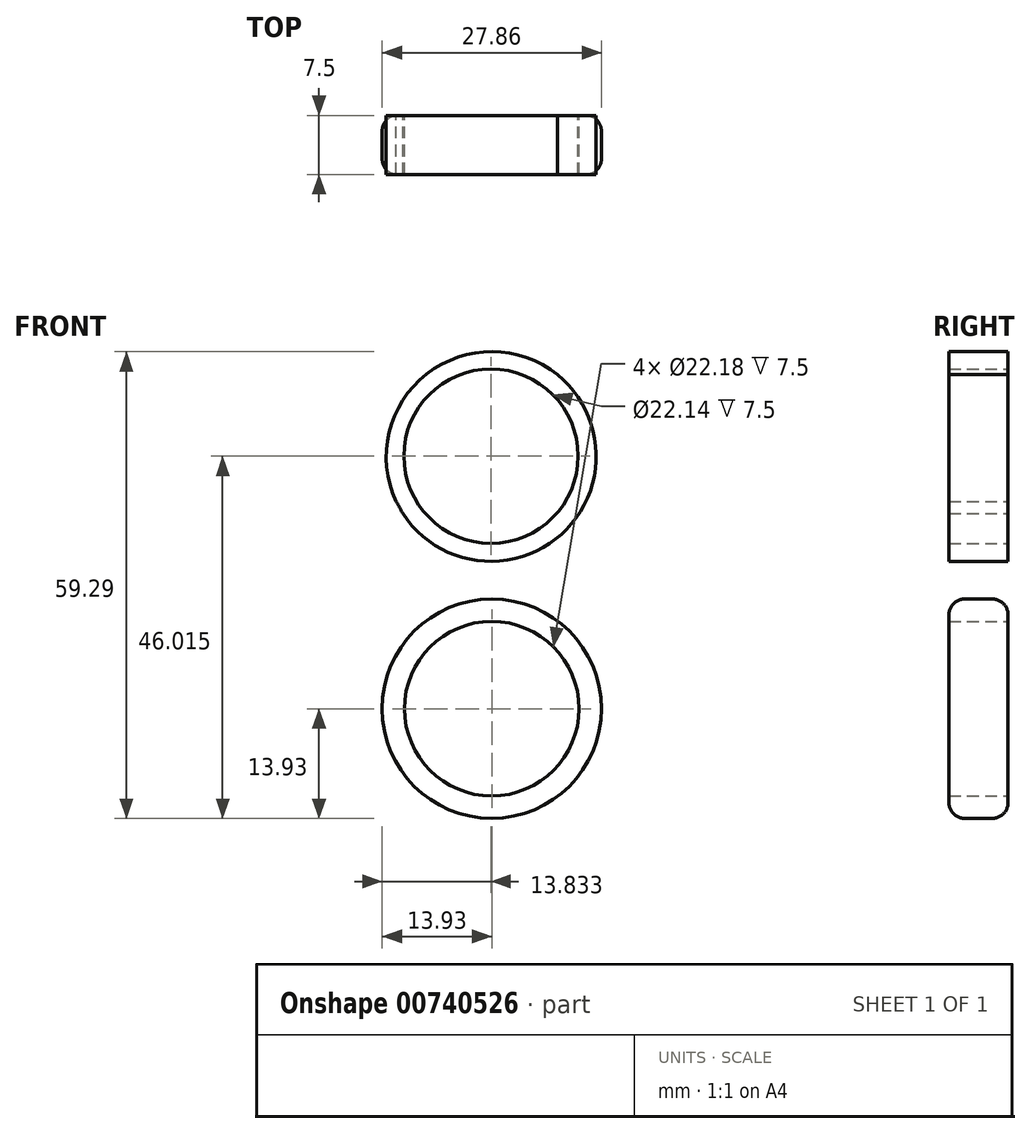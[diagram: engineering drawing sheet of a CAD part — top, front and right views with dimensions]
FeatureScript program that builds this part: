
annotation { "Feature Type Name" : "Feature", "Feature Type Description" : "" }
export const myFeature = defineFeature(function(context is Context, id is Id, definition is map)
    precondition{}
    {
        {
            var Q0;
            Q0=qCreatedBy(makeId("Front.planeOp"),FACE);
            var sketch = newSketch(context, id + "F0", { "sketchPlane" : qUnion([Q0])});
            skCircle(sketch, "E0", {"center": v(0, 0) * mm, "radius": 11.09 * mm});
            skCircle(sketch, "E1", {"center": v(0, 0) * mm, "radius": 13.93 * mm});
            skPoint(sketch, "E2.orphan", {"position": v(-13.93, 6.55) * mm});
            skPoint(sketch, "E3.first.point", {"position": v(-12.25, 30.96) * mm});
            skPoint(sketch, "E3.second.point", {"position": v(12.04, 33.37) * mm});
            skPoint(sketch, "E3.third.point", {"position": v(5.26, 21.12) * mm});
            skCircle(sketch, "E4", {"center": v(-0.1, 32.09) * mm, "radius": 11.07 * mm});
            skCircle(sketch, "E5", {"center": v(-0.1, 32.09) * mm, "radius": 13.37 * mm});
            skArc(sketch, "E6", {"start": v(-11.7, 7.56) * mm, "mid": v(-9.36, 17) * mm, "end": v(-12.16, 26.32) * mm});
            skPoint(sketch, "E6.startSnap0", {"position": v(-13.17, 7.56) * mm});
            skPoint(sketch, "E7.trimOffspring.end.orphan", {"position": v(-8.26, 23) * mm});
            skPoint(sketch, "E8.orphan", {"position": v(-10.96, 11.31) * mm});
            skPoint(sketch, "E9.orphan", {"position": v(10.96, 11.31) * mm});
            skPoint(sketch, "E10.MirrorCS.end.orphan", {"position": v(13.93, 3.28) * mm});
            skPoint(sketch, "E11.MirrorCS.end.orphan", {"position": v(8.26, 23) * mm});
            skArc(sketch, "E12.MirrorCS", {"start": v(11.7, 7.56) * mm, "mid": v(9.36, 17) * mm, "end": v(12.16, 26.32) * mm});
            skArc(sketch, "E13", {"start": v(12.16, 26.32) * mm, "mid": v(0, 45.36) * mm, "end": v(-12.16, 26.32) * mm});
            skArc(sketch, "E14", {"start": v(-11.7, 7.56) * mm, "mid": v(0, -12.58) * mm, "end": v(11.7, 7.56) * mm});
            skPoint(sketch, "E15.end.orphan", {"position": v(-13.93, 3.28) * mm});
            skPoint(sketch, "E15.start.orphan", {"position": v(-13.93, 0) * mm});
            skPoint(sketch, "E16.MirrorCS.start.orphan", {"position": v(13.93, 0) * mm});
            skSolve(sketch);
        }
        {
            var Q0;
            {var subQ0=sQuery(id+"F0.wireOp",EDGE,"E12.MirrorCS");Q0=makeQuery(id+"F0.imprint","IMPRINT",FACE,{"disambiguationData":[TD([[makeQuery(id+"F0.imprint","IMPRINT",EDGE,{"derivedFrom":subQ0}),1.0]])]});}
            var Q1;
            Q1=makeQuery(id+"F0.imprint","IMPRINT",FACE,{"disambiguationData":[TD([[makeQuery(id+"F0.imprint","IMPRINT",EDGE,{"derivedFrom":sQuery(id+"F0.wireOp",EDGE,"E4")}),-1.0]])]});
            var Q2;
            Q2=makeQuery(id+"F0.imprint","IMPRINT",FACE,{"disambiguationData":[TD([[makeQuery(id+"F0.imprint","IMPRINT",EDGE,{"derivedFrom":sQuery(id+"F0.wireOp",EDGE,"E0")}),-1.0]])]});
            var Q3;
            {var subQ0=sQuery(id+"F0.wireOp",EDGE,"E14");Q3=makeQuery(id+"F0.imprint","IMPRINT",FACE,{"disambiguationData":[TD([[makeQuery(id+"F0.imprint","IMPRINT",EDGE,{"derivedFrom":subQ0}),-1.0]])]});}
            extrude(context, id + "F1", {"entities" : qUnion([Q0, Q1, Q2, Q3]), "depth" : 7.5 * mm, "offsetDistance" : 25 * mm});
        }
        {
            var Q0;
            Q0=makeQuery(id+"F1.opExtrude","CAP_EDGE",EDGE,{"disambiguationData":[OSD([sQuery(id+"F0.wireOp",EDGE,"E13")])],"isStart":false});
            var Q1;
            Q1=makeQuery(id+"F1.opExtrude","CAP_EDGE",EDGE,{"disambiguationData":[OSD([sQuery(id+"F0.wireOp",EDGE,"E12.MirrorCS")])],"isStart":false});
            var Q2;
            Q2=makeQuery(id+"F1.opExtrude","CAP_EDGE",EDGE,{"disambiguationData":[OSD([sQuery(id+"F0.wireOp",EDGE,"E6")])],"isStart":false});
            var Q3;
            Q3=makeQuery(id+"F1.opExtrude","CAP_EDGE",EDGE,{"disambiguationData":[OSD([sQuery(id+"F0.wireOp",EDGE,"E1")])],"isStart":false});
            var Q4;
            Q4=makeQuery(id+"F1.opExtrude","CAP_EDGE",EDGE,{"disambiguationData":[OSD([sQuery(id+"F0.wireOp",EDGE,"E6")])],"isStart":true});
            var Q5;
            Q5=makeQuery(id+"F1.opExtrude","CAP_EDGE",EDGE,{"disambiguationData":[OSD([sQuery(id+"F0.wireOp",EDGE,"E1")])],"isStart":true});
            var Q6;
            Q6=makeQuery(id+"F1.opExtrude","CAP_EDGE",EDGE,{"disambiguationData":[OSD([sQuery(id+"F0.wireOp",EDGE,"E12.MirrorCS")])],"isStart":true});
            var Q7;
            Q7=makeQuery(id+"F1.opExtrude","CAP_EDGE",EDGE,{"disambiguationData":[OSD([sQuery(id+"F0.wireOp",EDGE,"E13")])],"isStart":true});
            fillet(context, id + "F2", {"entities" : qUnion([Q0, Q1, Q2, Q3, Q4, Q5, Q6, Q7]), "radius" : 2 * mm, "tangentPropagation" : true, "allowEdgeOverflow" : false});
        }
        {
            var Q0;
            Q0=makeQuery(id+"F1.opExtrude","SWEPT_BODY",BODY,{"disambiguationData":[OSD([sQuery(id+"F0.wireOp",EDGE,"E0"),sQuery(id+"F0.wireOp",EDGE,"E1"),sQuery(id+"F0.wireOp",EDGE,"E4"),sQuery(id+"F0.wireOp",EDGE,"E6"),sQuery(id+"F0.wireOp",EDGE,"E12.MirrorCS"),sQuery(id+"F0.wireOp",EDGE,"E13")])]});
            var Q1;
            Q1=makeQuery(id+"F1.opExtrude","CAP_EDGE",EDGE,{"disambiguationData":[OSD([sQuery(id+"F0.wireOp",EDGE,"E0")])],"isStart":false});
            transform(context, id + "F3", {"entities" : qUnion([Q0]), "transformType" : TransformType.ROTATION, "transformAxis" : qUnion([Q1]), "angle" : 90 * degree, "makeCopy" : true});
        }
        {
            var Q0;
            Q0=makeQuery(id+"F3.opPattern","COPY",BODY,{"derivedFrom":makeQuery(id+"F1.opExtrude","SWEPT_BODY",BODY,{"disambiguationData":[OSD([sQuery(id+"F0.wireOp",EDGE,"E0"),sQuery(id+"F0.wireOp",EDGE,"E1"),sQuery(id+"F0.wireOp",EDGE,"E4"),sQuery(id+"F0.wireOp",EDGE,"E6"),sQuery(id+"F0.wireOp",EDGE,"E12.MirrorCS"),sQuery(id+"F0.wireOp",EDGE,"E13")])]}),"instanceName":"1"});
            var Q1;
            Q1=makeQuery(id+"F1.opExtrude","CAP_EDGE",EDGE,{"disambiguationData":[OSD([sQuery(id+"F0.wireOp",EDGE,"E0")])],"isStart":false});
            transform(context, id + "F4", {"entities" : qUnion([Q0]), "transformType" : TransformType.ROTATION, "transformAxis" : qUnion([Q1]), "angle" : 90 * degree, "makeCopy" : true});
        }
        {
            var Q0;
            Q0=makeQuery(id+"F4.opPattern","COPY",BODY,{"derivedFrom":makeQuery(id+"F3.opPattern","COPY",BODY,{"derivedFrom":makeQuery(id+"F1.opExtrude","SWEPT_BODY",BODY,{"disambiguationData":[OSD([sQuery(id+"F0.wireOp",EDGE,"E0"),sQuery(id+"F0.wireOp",EDGE,"E1"),sQuery(id+"F0.wireOp",EDGE,"E4"),sQuery(id+"F0.wireOp",EDGE,"E6"),sQuery(id+"F0.wireOp",EDGE,"E12.MirrorCS"),sQuery(id+"F0.wireOp",EDGE,"E13")])]}),"instanceName":"1"}),"instanceName":"1"});
            var Q1;
            Q1=makeQuery(id+"F1.opExtrude","CAP_EDGE",EDGE,{"disambiguationData":[OSD([sQuery(id+"F0.wireOp",EDGE,"E0")])],"isStart":false});
            transform(context, id + "F5", {"entities" : qUnion([Q0]), "transformType" : TransformType.ROTATION, "transformAxis" : qUnion([Q1]), "angle" : 90 * degree, "makeCopy" : true});
        }
    });
